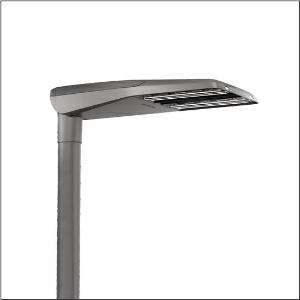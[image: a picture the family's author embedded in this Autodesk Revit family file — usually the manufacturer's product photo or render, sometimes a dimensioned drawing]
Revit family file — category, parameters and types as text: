
# Revit family: streetlight_sl_11_iq_midi___st1_0st0_5_5xc3j51f08me_a600
name_source: partatom
category: Lighting Fixtures
units: mm (PartAtom-declared; Revit-internal decimal feet)

## family parameters
Cut with Voids When Loaded = No
Host = Face
Light Source = No
Part Type = Normal
Room Calculation Point = No
Round Connector Dimension = Use Diameter
Shared = No

## types (1)
- --- (1 x LED, 17650 lm, 124.7 W, 3000K)
    Apparent Load = 125 VA
    CIE Flux Codes = 35 68 96 100 100
    Color Rendering = 70
    Color Temperature = 3000K
    Default Elevation = 1800 mm
    Description = Streetlight SL 11 iQ midi, mast luminaire, primary light control with 3 zone facetted reflector, of plastic, silver coated, highly specular, primary optical cover: cover, of PMMA, transparent, light distribution: ST1.0ST0.5, light emission: direct distribution, primary light characteristic: asymmetric, installation type: post-top, side-entry, LED, High Power LED, rated luminous flux: 17.650lm, luminous efficacy: 142lm/W, light colour: 730, colour temperature: 3000K, control: Street-Remote, Auto-Match, Temp-Guard, Lumen-Switch, Night-Set, Smart-Wire, Light-Fading, Desk-Remote (wireless, voltage-free reading and setting of iQ features in the workshop via application-optimized NFC function/RFID function), optimised constant luminous flux control (CLO 2.0), with cable H07RN-F 5x 1.5mm², mains connection: 230..240V, AC, 50/60Hz, connection cable pre-assembled, cable length: 12,5m, start of lifetime: 125W, end of service life: 132W, reduction: 57W, luminaire housing, of diecast aluminium, powder-coated, Siteco® metallic grey (DB 702S), please order mast flange separately, inclination adjustable without tools: 0°, 5°, 10°, 15° (post-top) | 0°, -5°, -10°, -15° (side-entry), sealing non-destructively replaceable, multi-level sealing system, length: 780mm, width: 376mm, height: 118mm, mast flange for spigot size: 42mm (side-entry): 5XC10008XM4, 60/48mm (side-entry/post-top): 5XC10108XM2, 76/60mm (side-entry/post-top): 5XC10108XM1, equipment: Power, protection rating (complete): IP66, insulation class (complete): insulation class II (safety insulation), certification: CE, ENEC, VDE, impact resistance: IK09, permissible operating ambient temperature for outdoor applications: -25..+50°C, standard-compliant lighting for roads and squares, Environmental Product Declaration (EPD) tested and certified by an independent institute, packaging unit: 1 piece

Light Distribution: ST1.0ST0.5
    Height = 118 mm
    Lamp = 1 x LED
    Lamp Light Flux = 17650 lm
    Lamp Power = 124.7 W
    Lamp count = 1
    Length = 780 mm
    Luminous efficacy = 142 lm/W
    Manufacturer = Siteco
    ModVariant = No
    Model = 5XC3J51F08ME
    Number of Poles = 1
    OnlyDefault = Yes
    Power Factor = 1
    Product Name = Streetlight SL 11 iQ midi | ST1.0ST0.5
    Product group = mast luminaire | pylon top
    ProductGroupID = 6100
    Protection Class = Protection class II
    Protection Degree = IP 66
    RLX_Detail_Level = 1
    RLX_Emergency_Light_Flux = 0 lm
    RLX_Emergency_Type = 0
    RLX_Emergency_Type_DB = No
    RlxData = <blob elided: 70649 chars, md5=7a1f4544>
    Socket = socket
    Standby Power = 0 W
    System Light Flux = 17650 lm
    System Power = 125 W
    Type Comments = factory setting: luminous flux: 100 % | dim-lin: 254 | 557 mA
    Type Image = l_1005960.jpg
    URL = http://relux.com
    VarID = @adj_002997
    Voltage = 0 V
    Weight = 0.00 kg
    Width = 376 mm

## geometry (parser evidence)
native form markers: Blend x4, Sweep x9
no freeform markers — native parametric forms only
